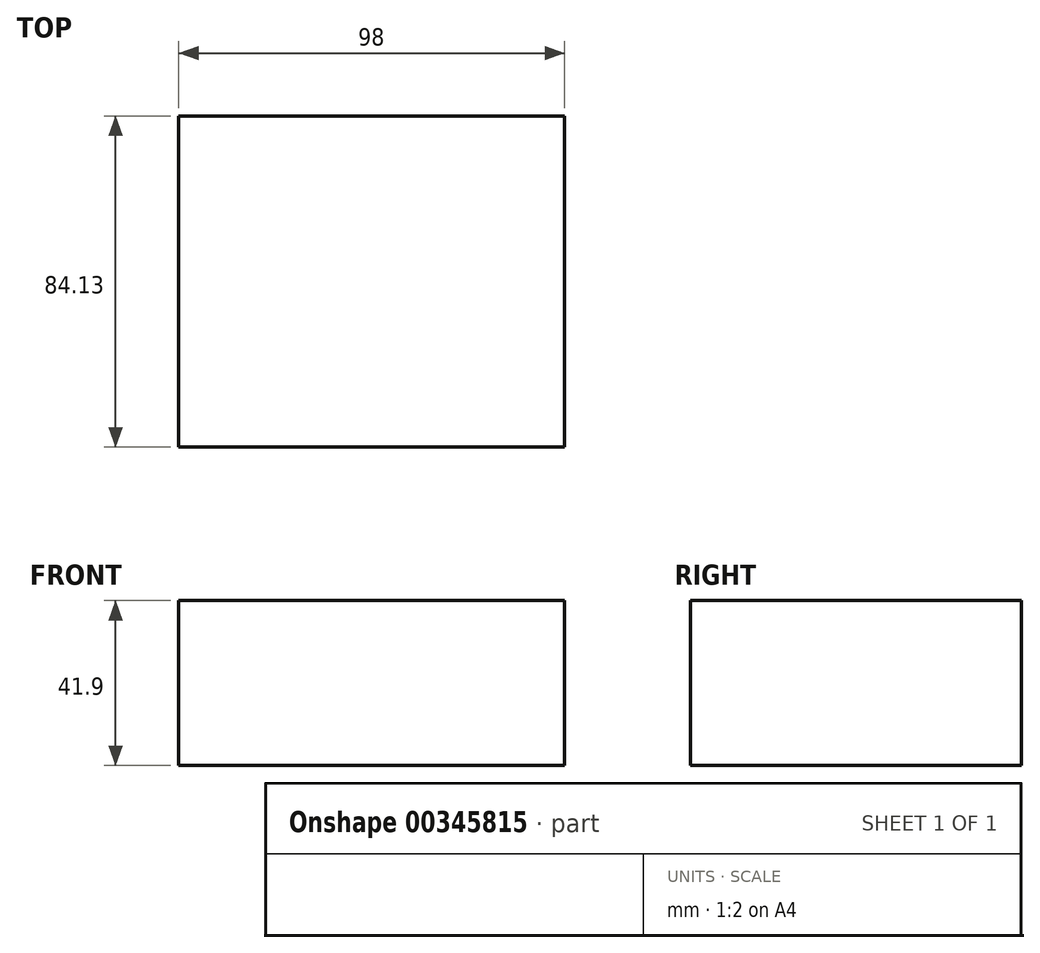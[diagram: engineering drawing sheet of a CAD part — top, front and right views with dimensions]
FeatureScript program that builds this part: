
annotation { "Feature Type Name" : "Feature", "Feature Type Description" : "" }
export const myFeature = defineFeature(function(context is Context, id is Id, definition is map)
    precondition{}
    {
        {
            var Q0;
            Q0=qCreatedBy(makeId("Top.planeOp"),FACE);
            var sketch = newSketch(context, id + "F0", { "sketchPlane" : qUnion([Q0])});
            skLineSegment(sketch, "E0.bottom", {"start": v(-46.42, 34.98) * mm, "end": v(51.58, 34.98) * mm});
            skLineSegment(sketch, "E0.top", {"start": v(-46.42, -49.15) * mm, "end": v(51.58, -49.15) * mm});
            skLineSegment(sketch, "E0.left", {"start": v(-46.42, 34.98) * mm, "end": v(-46.42, -49.15) * mm});
            skLineSegment(sketch, "E0.right", {"start": v(51.58, 34.98) * mm, "end": v(51.58, -49.15) * mm});
            skSolve(sketch);
        }
        {
            var Q0;
            Q0=makeQuery(id+"F0.imprint","IMPRINT",FACE,{"disambiguationData":[TD([[makeQuery(id+"F0.imprint","IMPRINT",EDGE,{"derivedFrom":sQuery(id+"F0.wireOp",EDGE,"E0.bottom")}),-1.0]])]});
            extrude(context, id + "F1", {"entities" : qUnion([Q0]), "depth" : 41.9 * mm});
        }
    });
